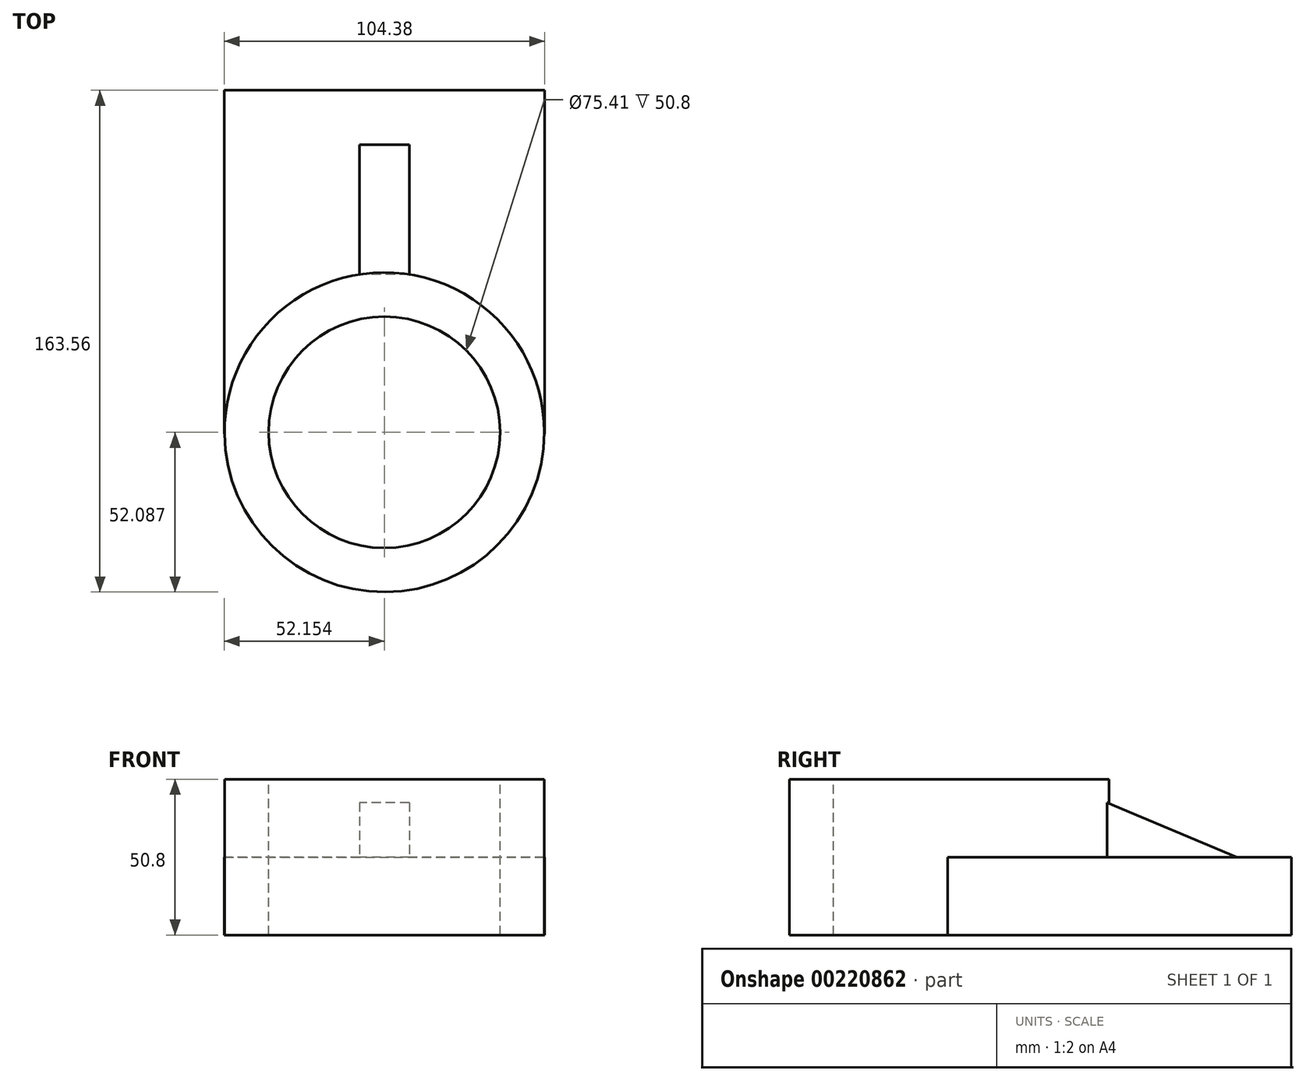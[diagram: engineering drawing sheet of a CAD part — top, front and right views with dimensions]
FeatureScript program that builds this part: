
annotation { "Feature Type Name" : "Feature", "Feature Type Description" : "" }
export const myFeature = defineFeature(function(context is Context, id is Id, definition is map)
    precondition{}
    {
        {
            var Q0;
            Q0=qCreatedBy(makeId("Top.planeOp"),FACE);
            var sketch = newSketch(context, id + "F0", { "sketchPlane" : qUnion([Q0])});
            skLineSegment(sketch, "E0.bottom", {"start": v(-52.19, 56) * mm, "end": v(52.19, 56) * mm});
            skLineSegment(sketch, "E0.top", {"start": v(-52.19, -56) * mm, "end": v(52.19, -56) * mm});
            skLineSegment(sketch, "E0.left", {"start": v(-52.19, 56) * mm, "end": v(-52.19, -56) * mm});
            skLineSegment(sketch, "E0.right", {"start": v(52.19, 56) * mm, "end": v(52.19, -56) * mm});
            skPoint(sketch, "E0.middle", {"position": v(0, 0) * mm});
            skSolve(sketch);
        }
        {
            var Q0;
            Q0=qCreatedBy(makeId("Top.planeOp"),FACE);
            var sketch = newSketch(context, id + "F1", { "sketchPlane" : qUnion([Q0])});
            skCircle(sketch, "E1", {"center": v(-0.04, -55.47) * mm, "radius": 52.09 * mm});
            skPoint(sketch, "E1.first.point", {"position": v(-52.12, -55.8) * mm});
            skPoint(sketch, "E1.second.point", {"position": v(52.05, -56.13) * mm});
            skPoint(sketch, "E1.third.point", {"position": v(-52.12, -55.15) * mm});
            skSolve(sketch);
        }
        {
            var Q0;
            Q0 = qSketchRegion(id + "F0", true);
            extrude(context, id + "F2", {"entities" : qUnion([Q0]), "depth" : 25.4 * mm});
        }
        {
            var Q0;
            Q0 = qSketchRegion(id + "F1", true);
            extrude(context, id + "F3", {"entities" : qUnion([Q0]), "operationType" : NewBodyOperationType.ADD, "depth" : 50.8 * mm});
        }
        {
            var Q0;
            Q0=makeQuery(id+"F3.opExtrude","CAP_FACE",FACE,{"disambiguationData":[OSD([sQuery(id+"F1.wireOp",EDGE,"E1")])],"isStart":false});
            var sketch = newSketch(context, id + "F4", { "sketchPlane" : qUnion([Q0])});
            skCircle(sketch, "E2", {"center": v(-0.04, -55.47) * mm, "radius": 37.7 * mm});
            skSolve(sketch);
        }
        {
            var Q0;
            Q0=makeQuery(id+"F4.imprint","IMPRINT",FACE,{"disambiguationData":[TD([[makeQuery(id+"F4.imprint","IMPRINT",EDGE,{"derivedFrom":sQuery(id+"F4.wireOp",EDGE,"E2")}),1.0]])]});
            extrude(context, id + "F5", {"entities" : qUnion([Q0]), "operationType" : NewBodyOperationType.REMOVE, "endBound" : BoundingType.THROUGH_ALL, "oppositeDirection" : true, "depth" : 50.8 * mm});
        }
        {
            var Q0;
            Q0=makeQuery(id+"F2.opExtrude","CAP_FACE",FACE,{"disambiguationData":[OSD([sQuery(id+"F0.wireOp",EDGE,"E0.bottom"),sQuery(id+"F0.wireOp",EDGE,"E0.top"),sQuery(id+"F0.wireOp",EDGE,"E0.left"),sQuery(id+"F0.wireOp",EDGE,"E0.right")])],"isStart":false});
            var sketch = newSketch(context, id + "F6", { "sketchPlane" : qUnion([Q0])});
            skLineSegment(sketch, "E3.bottom", {"start": v(8.1, -4.02) * mm, "end": v(-8.1, -4.02) * mm});
            skLineSegment(sketch, "E3.top", {"start": v(8.1, 38.28) * mm, "end": v(-8.1, 38.28) * mm});
            skLineSegment(sketch, "E3.left", {"start": v(8.1, -4.02) * mm, "end": v(8.1, 38.28) * mm});
            skLineSegment(sketch, "E3.right", {"start": v(-8.1, -4.02) * mm, "end": v(-8.1, 38.28) * mm});
            skPoint(sketch, "E3.middle", {"position": v(0, 17.13) * mm});
            skSolve(sketch);
        }
        {
            var Q0;
            {var subQ0=sQuery(id+"F6.wireOp",EDGE,"E3.top");Q0=makeQuery(id+"F6.imprint","IMPRINT",FACE,{"disambiguationData":[TD([[makeQuery(id+"F6.imprint","IMPRINT",EDGE,{"derivedFrom":subQ0}),1.0]])]});}
            extrude(context, id + "F7", {"entities" : qUnion([Q0]), "operationType" : NewBodyOperationType.ADD, "depth" : 17.78 * mm});
        }
        {
            var Q0;
            Q0=makeQuery(id+"F7.opExtrude","SWEPT_FACE",FACE,{"disambiguationData":[OSD([sQuery(id+"F6.wireOp",EDGE,"E3.right")])]});
            var sketch = newSketch(context, id + "F8", { "sketchPlane" : qUnion([Q0])});
            skLineSegment(sketch, "E4", {"start": v(-38.28, 25.4) * mm, "end": v(4.01, 43.18) * mm});
            skSolve(sketch);
        }
        {
            var Q0;
            Q0=makeQuery(id+"F8.imprint","IMPRINT",FACE,{"disambiguationData":[TD([[makeQuery(id+"F8.imprint","IMPRINT",EDGE,{"derivedFrom":sQuery(id+"F8.wireOp",EDGE,"E4")}),1.0]])]});
            extrude(context, id + "F9", {"entities" : qUnion([Q0]), "operationType" : NewBodyOperationType.REMOVE, "endBound" : BoundingType.THROUGH_ALL, "oppositeDirection" : true, "depth" : 25.4 * mm});
        }
    });
